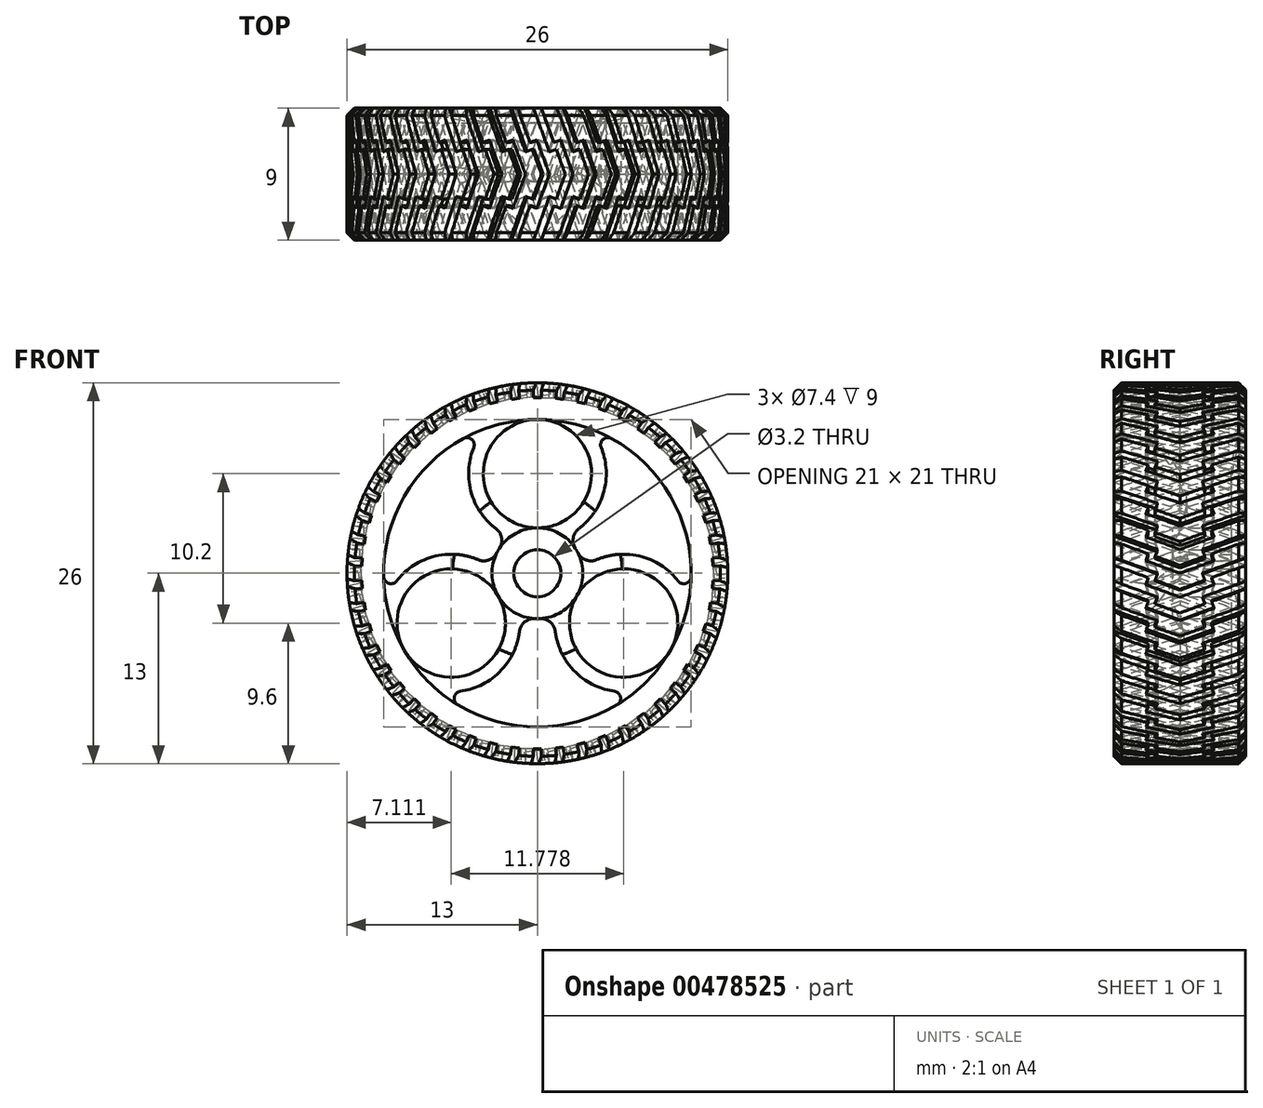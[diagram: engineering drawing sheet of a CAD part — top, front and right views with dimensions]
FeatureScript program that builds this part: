
annotation { "Feature Type Name" : "Feature", "Feature Type Description" : "" }
export const myFeature = defineFeature(function(context is Context, id is Id, definition is map)
    precondition{}
    {
        {
            var Q0;
            Q0=qCreatedBy(makeId("Right.planeOp"),FACE);
            var sketch = newSketch(context, id + "F0", { "sketchPlane" : qUnion([Q0])});
            skLineSegment(sketch, "E0", {"start": v(4.5, 13) * mm, "end": v(4.5, 10.5) * mm});
            skLineSegment(sketch, "E1", {"start": v(4.5, 10.5) * mm, "end": v(-4.5, 10.5) * mm});
            skLineSegment(sketch, "E2", {"start": v(-4.5, 10.5) * mm, "end": v(-4.5, 13) * mm});
            skLineSegment(sketch, "E3", {"start": v(-4.5, 13) * mm, "end": v(4.5, 13) * mm});
            skLineSegment(sketch, "E4", {"start": v(0, 4.58) * mm, "end": v(0, -2.9) * mm, "construction": true});
            skLineSegment(sketch, "E5", {"start": v(3.7, 0) * mm, "end": v(-3.86, 0) * mm, "construction": true});
            skLineSegment(sketch, "E6", {"start": v(3.5, 3.1) * mm, "end": v(3.5, 1.6) * mm});
            skLineSegment(sketch, "E7", {"start": v(3.5, 1.6) * mm, "end": v(0.5, 1.6) * mm});
            skLineSegment(sketch, "E8", {"start": v(0.5, 1.6) * mm, "end": v(0.5, 3.1) * mm});
            skLineSegment(sketch, "E9", {"start": v(0.5, 3.1) * mm, "end": v(3.5, 3.1) * mm});
            skSolve(sketch);
        }
        {
            var Q0;
            Q0=makeQuery(id+"F0.imprint","IMPRINT",FACE,{"disambiguationData":[TD([[makeQuery(id+"F0.imprint","IMPRINT",EDGE,{"derivedFrom":sQuery(id+"F0.wireOp",EDGE,"E0")}),-1.0]])]});
            var Q1;
            Q1=makeQuery(id+"F0.imprint","IMPRINT",FACE,{"disambiguationData":[TD([[makeQuery(id+"F0.imprint","IMPRINT",EDGE,{"derivedFrom":sQuery(id+"F0.wireOp",EDGE,"E6")}),-1.0]])]});
            var Q2;
            Q2=sQuery(id+"F0.wireOp",EDGE,"E5");
            revolve(context, id + "F1", {"entities" : qUnion([Q0, Q1]), "axis" : qUnion([Q2]), "revolveType" : RevolveType.FULL});
        }
        {
            var Q0;
            Q0=makeQuery(id+"F1.opRevolve","SWEPT_FACE",FACE,{"disambiguationData":[OSD([sQuery(id+"F0.wireOp",EDGE,"E6")])]});
            var sketch = newSketch(context, id + "F2", { "sketchPlane" : qUnion([Q0])});
            skCircle(sketch, "E10", {"center": v(0, 6.8) * mm, "radius": 4.7 * mm});
            skCircle(sketch, "E11", {"center": v(0, 6.8) * mm, "radius": 3.7 * mm});
            skLineSegment(sketch, "E12", {"start": v(5.5, 10.5) * mm, "end": v(-6.08, 10.5) * mm, "construction": true});
            skLineSegment(sketch, "E13", {"start": v(-5.55, 11.5) * mm, "end": v(4.86, 11.5) * mm, "construction": true});
            skSolve(sketch);
        }
        {
            var Q0;
            {var subQ4=sQuery(id+"F2.wireOp",EDGE,"E11");Q0=makeQuery(id+"F2.imprint","IMPRINT",FACE,{"disambiguationData":[TD([[makeQuery(id+"F2.imprint","IMPRINT",EDGE,{"derivedFrom":subQ4}),-1.0]])]});}
            var Q1;
            {var subQ0=sQuery(id+"F2.wireOp",EDGE,"E10");var subQ1=makeQuery(id+"F1.opRevolve","SWEPT_EDGE",EDGE,{"disambiguationData":[OSD([sQuery(id+"F0.wireOp",EDGE,"E6"),sQuery(id+"F0.wireOp",EDGE,"E9")])]});var subQ2=makeQuery(id+"F2.imprint","INTERSECT",VERTEX,{"disambiguationData":[OD(0.0)],"derivedFrom":[subQ1,subQ0]});Q1=makeQuery(id+"F2.imprint","IMPRINT",FACE,{"disambiguationData":[TD([[makeQuery(id+"F2.imprint","IMPRINT",EDGE,{"disambiguationData":[TD([[subQ2,1.0]])],"derivedFrom":subQ0}),1.0]])]});}
            var Q2;
            Q2=makeQuery(id+"F1.opRevolve","SWEPT_FACE",FACE,{"disambiguationData":[OSD([sQuery(id+"F0.wireOp",EDGE,"E8")])]});
            extrude(context, id + "F3", {"entities" : qUnion([Q0, Q1]), "endBound" : BoundingType.UP_TO_SURFACE, "oppositeDirection" : true, "endBoundEntityFace" : qUnion([Q2]), "depth" : 5 * mm});
        }
        {
            var Q0;
            Q0=makeQuery(id+"F3.opExtrude","SWEPT_BODY",BODY,{"disambiguationData":[OSD([sQuery(id+"F2.wireOp",EDGE,"E10"),sQuery(id+"F2.wireOp",EDGE,"E11")])]});
            var Q1;
            Q1=makeQuery(id+"F1.opRevolve","SWEPT_FACE",FACE,{"disambiguationData":[OSD([sQuery(id+"F0.wireOp",EDGE,"E9")])]});
            circularPattern(context, id + "F4", {"entities" : qUnion([Q0]), "axis" : qUnion([Q1]), "angle" : 360 * degree, "instanceCount" : 3, "equalSpace" : true});
        }
        {
            var Q0;
            Q0=makeQuery(id+"F3.opExtrude","SWEPT_BODY",BODY,{"disambiguationData":[OSD([sQuery(id+"F2.wireOp",EDGE,"E10"),sQuery(id+"F2.wireOp",EDGE,"E11")])]});
            var Q1;
            Q1=makeQuery(id+"F4.opPattern","COPY",BODY,{"derivedFrom":makeQuery(id+"F3.opExtrude","SWEPT_BODY",BODY,{"disambiguationData":[OSD([sQuery(id+"F2.wireOp",EDGE,"E10"),sQuery(id+"F2.wireOp",EDGE,"E11")])]}),"instanceName":"4"});
            var Q2;
            Q2=makeQuery(id+"F4.opPattern","COPY",BODY,{"derivedFrom":makeQuery(id+"F3.opExtrude","SWEPT_BODY",BODY,{"disambiguationData":[OSD([sQuery(id+"F2.wireOp",EDGE,"E10"),sQuery(id+"F2.wireOp",EDGE,"E11")])]}),"instanceName":"3"});
            var Q3;
            Q3=makeQuery(id+"F4.opPattern","COPY",BODY,{"derivedFrom":makeQuery(id+"F3.opExtrude","SWEPT_BODY",BODY,{"disambiguationData":[OSD([sQuery(id+"F2.wireOp",EDGE,"E10"),sQuery(id+"F2.wireOp",EDGE,"E11")])]}),"instanceName":"2"});
            var Q4;
            Q4=makeQuery(id+"F4.opPattern","COPY",BODY,{"derivedFrom":makeQuery(id+"F3.opExtrude","SWEPT_BODY",BODY,{"disambiguationData":[OSD([sQuery(id+"F2.wireOp",EDGE,"E10"),sQuery(id+"F2.wireOp",EDGE,"E11")])]}),"instanceName":"1"});
            var Q5;
            Q5=makeQuery(id+"F1.opRevolve","SWEPT_BODY",BODY,{"disambiguationData":[OSD([sQuery(id+"F0.wireOp",EDGE,"E6"),sQuery(id+"F0.wireOp",EDGE,"E7"),sQuery(id+"F0.wireOp",EDGE,"E8"),sQuery(id+"F0.wireOp",EDGE,"E9")])]});
            booleanBodies(context, id + "F5", {"operationType" : BooleanOperationType.UNION, "tools" : qUnion([Q0, Q1, Q2, Q3, Q4, Q5])});
        }
        {
            var Q0;
            Q0=makeQuery(id+"F3.opExtrude","SWEPT_BODY",BODY,{"disambiguationData":[OSD([sQuery(id+"F2.wireOp",EDGE,"E10"),sQuery(id+"F2.wireOp",EDGE,"E11")])]});
            var Q1;
            Q1=makeQuery(id+"F1.opRevolve","SWEPT_BODY",BODY,{"disambiguationData":[OSD([sQuery(id+"F0.wireOp",EDGE,"E0"),sQuery(id+"F0.wireOp",EDGE,"E1"),sQuery(id+"F0.wireOp",EDGE,"E2"),sQuery(id+"F0.wireOp",EDGE,"E3")])]});
            booleanBodies(context, id + "F6", {"operationType" : BooleanOperationType.UNION, "tools" : qUnion([Q0, Q1])});
        }
        {
            var Q0;
            {var subQ0=sQuery(id+"F0.wireOp",EDGE,"E0");var subQ1=sQuery(id+"F0.wireOp",EDGE,"E3");Q0=makeQuery(id+"F11.boolean.opBoolean","SPLIT",EDGE,{"disambiguationData":[TD([makeQuery(id+"F11.opPattern","COPY",FACE,{"derivedFrom":makeQuery(id+"F10.opExtrude","SWEPT_FACE",FACE,{"disambiguationData":[OSD([sQuery(id+"F9.wireOp",EDGE,"E14")])]}),"instanceName":"47"})])],"derivedFrom":makeQuery(id+"F1.opRevolve","SWEPT_EDGE",EDGE,{"disambiguationData":[OSD([subQ0,subQ1])]})});}
            var Q1;
            Q1=makeQuery(id+"F1.opRevolve","SWEPT_EDGE",EDGE,{"disambiguationData":[OSD([sQuery(id+"F0.wireOp",EDGE,"E2"),sQuery(id+"F0.wireOp",EDGE,"E3")])]});
            chamfer(context, id + "F7", {"entities" : qUnion([Q0, Q1]), "width" : .5 * mm, "tangentPropagation" : true});
        }
        {
            var Q0;
            Q0=qCreatedBy(makeId("Top.planeOp"),FACE);
            cPlane(context, id + "F8", {"entities" : qUnion([Q0]), "cplaneType" : CPlaneType.OFFSET, "offset" : 26 / 2 * mm, "width" : 150 * mm, "height" : 150 * mm});
        }
        {
            var Q0;
            Q0=qCreatedBy(id+"F8.planeOp",FACE);
            var sketch = newSketch(context, id + "F9", { "sketchPlane" : qUnion([Q0])});
            skLineSegment(sketch, "E14", {"start": v(0.27, 4.5) * mm, "end": v(1.12, 2.16) * mm});
            skLineSegment(sketch, "E15", {"start": v(1.59, 2.34) * mm, "end": v(1.12, 2.16) * mm});
            skLineSegment(sketch, "E16", {"start": v(1.59, 2.34) * mm, "end": v(2.44, 0) * mm});
            skLineSegment(sketch, "E17", {"start": v(-13.36, 0) * mm, "end": v(12.93, 0) * mm, "construction": true});
            skLineSegment(sketch, "E18", {"start": v(-0.27, 4.5) * mm, "end": v(0.82, 1.52) * mm});
            skLineSegment(sketch, "E19", {"start": v(0.82, 1.52) * mm, "end": v(1.29, 1.7) * mm});
            skLineSegment(sketch, "E20", {"start": v(1.29, 1.7) * mm, "end": v(1.9, 0) * mm});
            skLineSegment(sketch, "E21", {"start": v(-0.27, 4.5) * mm, "end": v(0.27, 4.5) * mm});
            skPoint(sketch, "E22", {"position": v(0, 4.5) * mm});
            skLineSegment(sketch, "E23.MirrorCS", {"start": v(1.59, -2.34) * mm, "end": v(2.44, 0) * mm});
            skLineSegment(sketch, "E24.MirrorCS", {"start": v(1.29, -1.7) * mm, "end": v(1.9, 0) * mm});
            skLineSegment(sketch, "E25.MirrorCS", {"start": v(0.82, -1.52) * mm, "end": v(1.29, -1.7) * mm});
            skLineSegment(sketch, "E26.MirrorCS", {"start": v(1.59, -2.34) * mm, "end": v(1.12, -2.16) * mm});
            skLineSegment(sketch, "E27.MirrorCS", {"start": v(0.27, -4.5) * mm, "end": v(1.12, -2.16) * mm});
            skLineSegment(sketch, "E28.MirrorCS", {"start": v(-0.27, -4.5) * mm, "end": v(0.82, -1.52) * mm});
            skLineSegment(sketch, "E29.MirrorCS", {"start": v(-0.27, -4.5) * mm, "end": v(0.27, -4.5) * mm});
            skLineSegment(sketch, "E30.0", {"start": v(-12.5, 4.5) * mm, "end": v(12.5, 4.5) * mm});
            skLineSegment(sketch, "E31.0", {"start": v(12.5, -4.5) * mm, "end": v(-12.5, -4.5) * mm});
            skSolve(sketch);
        }
        {
            var Q0;
            Q0=makeQuery(id+"F9.imprint","IMPRINT",FACE,{"disambiguationData":[TD([[makeQuery(id+"F9.imprint","IMPRINT",EDGE,{"derivedFrom":sQuery(id+"F9.wireOp",EDGE,"E14")}),-1.0]])]});
            extrude(context, id + "F10", {"entities" : qUnion([Q0]), "oppositeDirection" : true, "depth" : 1 * mm});
        }
        {
            var Q0;
            Q0=makeQuery(id+"F10.opExtrude","SWEPT_BODY",BODY,{"disambiguationData":[OSD([sQuery(id+"F9.wireOp",EDGE,"E14"),sQuery(id+"F9.wireOp",EDGE,"E15"),sQuery(id+"F9.wireOp",EDGE,"E16"),sQuery(id+"F9.wireOp",EDGE,"E18"),sQuery(id+"F9.wireOp",EDGE,"E19"),sQuery(id+"F9.wireOp",EDGE,"E20"),sQuery(id+"F9.wireOp",EDGE,"E21"),sQuery(id+"F9.wireOp",EDGE,"E23.MirrorCS"),sQuery(id+"F9.wireOp",EDGE,"E24.MirrorCS"),sQuery(id+"F9.wireOp",EDGE,"E25.MirrorCS"),sQuery(id+"F9.wireOp",EDGE,"E26.MirrorCS"),sQuery(id+"F9.wireOp",EDGE,"E27.MirrorCS"),sQuery(id+"F9.wireOp",EDGE,"E28.MirrorCS"),sQuery(id+"F9.wireOp",EDGE,"E29.MirrorCS")])]});
            var Q1;
            Q1=makeQuery(id+"F1.opRevolve","SWEPT_FACE",FACE,{"disambiguationData":[OSD([sQuery(id+"F0.wireOp",EDGE,"E3")])]});
            var Q2;
            Q2=makeQuery(id+"F3.opExtrude","SWEPT_BODY",BODY,{"disambiguationData":[OSD([sQuery(id+"F2.wireOp",EDGE,"E10"),sQuery(id+"F2.wireOp",EDGE,"E11")])]});
            circularPattern(context, id + "F11", {"operationType" : NewBodyOperationType.REMOVE, "entities" : qUnion([Q0]), "axis" : qUnion([Q1]), "angle" : 360 * degree, "instanceCount" : 50, "equalSpace" : true});
        }
        {
            var Q0;
            {var subQ0=sQuery(id+"F0.wireOp",EDGE,"E8");var subQ1=makeQuery(id+"F3.opExtrude","CAP_FACE",FACE,{"disambiguationData":[OSD([subQ0])],"isStart":false});Q0=makeQuery(id+"F5.opBoolean","MERGE",FACE,{"derivedFrom":[makeQuery(id+"F1.opRevolve","SWEPT_FACE",FACE,{"disambiguationData":[OSD([subQ0])]}),subQ1,makeQuery(id+"F4.opPattern","COPY",FACE,{"derivedFrom":subQ1,"instanceName":"1"}),makeQuery(id+"F4.opPattern","COPY",FACE,{"derivedFrom":subQ1,"instanceName":"2"}),makeQuery(id+"F4.opPattern","COPY",FACE,{"derivedFrom":subQ1,"instanceName":"3"}),makeQuery(id+"F4.opPattern","COPY",FACE,{"derivedFrom":subQ1,"instanceName":"4"})]});}
            var sketch = newSketch(context, id + "F12", { "sketchPlane" : qUnion([Q0])});
            skCircle(sketch, "E32", {"center": v(0, 0) * mm, "radius": 1.6 * mm});
            skCircle(sketch, "E33", {"center": v(0, 0) * mm, "radius": 3.1 * mm});
            skSolve(sketch);
        }
        {
            var Q0;
            Q0=makeQuery(id+"F12.imprint","IMPRINT",FACE,{"disambiguationData":[TD([[makeQuery(id+"F12.imprint","IMPRINT",EDGE,{"derivedFrom":sQuery(id+"F12.wireOp",EDGE,"E32")}),1.0]])]});
            extrude(context, id + "F13", {"entities" : qUnion([Q0]), "operationType" : NewBodyOperationType.ADD, "depth" : 1 * mm});
        }
        {
            var Q0;
            Q0=makeQuery(id+"F6.opBoolean","INTERSECT",EDGE,{"disambiguationData":[OD(0.0)],"derivedFrom":[makeQuery(id+"F1.opRevolve","SWEPT_FACE",FACE,{"disambiguationData":[OSD([sQuery(id+"F0.wireOp",EDGE,"E1")])]}),makeQuery(id+"F4.opPattern","COPY",FACE,{"derivedFrom":makeQuery(id+"F3.opExtrude","SWEPT_FACE",FACE,{"disambiguationData":[OSD([sQuery(id+"F2.wireOp",EDGE,"E10")])]}),"instanceName":"2"})]});
            var Q1;
            Q1=makeQuery(id+"F6.opBoolean","INTERSECT",EDGE,{"disambiguationData":[OD(1.0)],"derivedFrom":[makeQuery(id+"F1.opRevolve","SWEPT_FACE",FACE,{"disambiguationData":[OSD([sQuery(id+"F0.wireOp",EDGE,"E1")])]}),makeQuery(id+"F4.opPattern","COPY",FACE,{"derivedFrom":makeQuery(id+"F3.opExtrude","SWEPT_FACE",FACE,{"disambiguationData":[OSD([sQuery(id+"F2.wireOp",EDGE,"E10")])]}),"instanceName":"2"})]});
            var Q2;
            Q2=makeQuery(id+"F6.opBoolean","INTERSECT",EDGE,{"disambiguationData":[OD(1.0)],"derivedFrom":[makeQuery(id+"F1.opRevolve","SWEPT_FACE",FACE,{"disambiguationData":[OSD([sQuery(id+"F0.wireOp",EDGE,"E1")])]}),makeQuery(id+"F4.opPattern","COPY",FACE,{"derivedFrom":makeQuery(id+"F3.opExtrude","SWEPT_FACE",FACE,{"disambiguationData":[OSD([sQuery(id+"F2.wireOp",EDGE,"E10")])]}),"instanceName":"1"})]});
            var Q3;
            Q3=makeQuery(id+"F6.opBoolean","INTERSECT",EDGE,{"disambiguationData":[OD(0.0)],"derivedFrom":[makeQuery(id+"F1.opRevolve","SWEPT_FACE",FACE,{"disambiguationData":[OSD([sQuery(id+"F0.wireOp",EDGE,"E1")])]}),makeQuery(id+"F3.opExtrude","SWEPT_FACE",FACE,{"disambiguationData":[OSD([sQuery(id+"F2.wireOp",EDGE,"E10")])]})]});
            var Q4;
            Q4=makeQuery(id+"F6.opBoolean","INTERSECT",EDGE,{"disambiguationData":[OD(1.0)],"derivedFrom":[makeQuery(id+"F1.opRevolve","SWEPT_FACE",FACE,{"disambiguationData":[OSD([sQuery(id+"F0.wireOp",EDGE,"E1")])]}),makeQuery(id+"F3.opExtrude","SWEPT_FACE",FACE,{"disambiguationData":[OSD([sQuery(id+"F2.wireOp",EDGE,"E10")])]})]});
            var Q5;
            Q5=makeQuery(id+"F6.opBoolean","INTERSECT",EDGE,{"disambiguationData":[OD(0.0)],"derivedFrom":[makeQuery(id+"F1.opRevolve","SWEPT_FACE",FACE,{"disambiguationData":[OSD([sQuery(id+"F0.wireOp",EDGE,"E1")])]}),makeQuery(id+"F4.opPattern","COPY",FACE,{"derivedFrom":makeQuery(id+"F3.opExtrude","SWEPT_FACE",FACE,{"disambiguationData":[OSD([sQuery(id+"F2.wireOp",EDGE,"E10")])]}),"instanceName":"1"})]});
            fillet(context, id + "F14", {"entities" : qUnion([Q0, Q1, Q2, Q3, Q4, Q5]), "radius" : .5 * mm, "tangentPropagation" : true, "allowEdgeOverflow" : false});
        }
        {
            var Q0;
            Q0=makeQuery(id+"F5.opBoolean","INTERSECT",EDGE,{"disambiguationData":[OD(0.0)],"derivedFrom":[makeQuery(id+"F1.opRevolve","SWEPT_FACE",FACE,{"disambiguationData":[OSD([sQuery(id+"F0.wireOp",EDGE,"E9")])]}),makeQuery(id+"F4.opPattern","COPY",FACE,{"derivedFrom":makeQuery(id+"F3.opExtrude","SWEPT_FACE",FACE,{"disambiguationData":[OSD([sQuery(id+"F2.wireOp",EDGE,"E10")])]}),"instanceName":"1"})]});
            var Q1;
            Q1=makeQuery(id+"F5.opBoolean","INTERSECT",EDGE,{"disambiguationData":[OD(1.0)],"derivedFrom":[makeQuery(id+"F1.opRevolve","SWEPT_FACE",FACE,{"disambiguationData":[OSD([sQuery(id+"F0.wireOp",EDGE,"E9")])]}),makeQuery(id+"F4.opPattern","COPY",FACE,{"derivedFrom":makeQuery(id+"F3.opExtrude","SWEPT_FACE",FACE,{"disambiguationData":[OSD([sQuery(id+"F2.wireOp",EDGE,"E10")])]}),"instanceName":"1"})]});
            var Q2;
            Q2=makeQuery(id+"F5.opBoolean","INTERSECT",EDGE,{"disambiguationData":[OD(1.0)],"derivedFrom":[makeQuery(id+"F1.opRevolve","SWEPT_FACE",FACE,{"disambiguationData":[OSD([sQuery(id+"F0.wireOp",EDGE,"E9")])]}),makeQuery(id+"F3.opExtrude","SWEPT_FACE",FACE,{"disambiguationData":[OSD([sQuery(id+"F2.wireOp",EDGE,"E10")])]})]});
            var Q3;
            Q3=makeQuery(id+"F5.opBoolean","INTERSECT",EDGE,{"disambiguationData":[OD(0.0)],"derivedFrom":[makeQuery(id+"F1.opRevolve","SWEPT_FACE",FACE,{"disambiguationData":[OSD([sQuery(id+"F0.wireOp",EDGE,"E9")])]}),makeQuery(id+"F4.opPattern","COPY",FACE,{"derivedFrom":makeQuery(id+"F3.opExtrude","SWEPT_FACE",FACE,{"disambiguationData":[OSD([sQuery(id+"F2.wireOp",EDGE,"E10")])]}),"instanceName":"2"})]});
            var Q4;
            Q4=makeQuery(id+"F5.opBoolean","INTERSECT",EDGE,{"disambiguationData":[OD(1.0)],"derivedFrom":[makeQuery(id+"F1.opRevolve","SWEPT_FACE",FACE,{"disambiguationData":[OSD([sQuery(id+"F0.wireOp",EDGE,"E9")])]}),makeQuery(id+"F4.opPattern","COPY",FACE,{"derivedFrom":makeQuery(id+"F3.opExtrude","SWEPT_FACE",FACE,{"disambiguationData":[OSD([sQuery(id+"F2.wireOp",EDGE,"E10")])]}),"instanceName":"2"})]});
            var Q5;
            Q5=makeQuery(id+"F5.opBoolean","INTERSECT",EDGE,{"disambiguationData":[OD(0.0)],"derivedFrom":[makeQuery(id+"F1.opRevolve","SWEPT_FACE",FACE,{"disambiguationData":[OSD([sQuery(id+"F0.wireOp",EDGE,"E9")])]}),makeQuery(id+"F3.opExtrude","SWEPT_FACE",FACE,{"disambiguationData":[OSD([sQuery(id+"F2.wireOp",EDGE,"E10")])]})]});
            fillet(context, id + "F15", {"entities" : qUnion([Q0, Q1, Q2, Q3, Q4, Q5]), "radius" : 1 * mm, "tangentPropagation" : true, "allowEdgeOverflow" : false});
        }
        {
            var Q0;
            {var subQ0=sQuery(id+"F0.wireOp",EDGE,"E8");var subQ1=makeQuery(id+"F3.opExtrude","CAP_FACE",FACE,{"disambiguationData":[OSD([subQ0])],"isStart":false});var subQ2=sQuery(id+"F12.wireOp",EDGE,"E33");Q0=makeQuery(id+"F13.boolean.opBoolean","SPLIT",EDGE,{"disambiguationData":[TD([makeQuery(id+"F1.opRevolve","SWEPT_FACE",FACE,{"disambiguationData":[OSD([subQ0])]}),makeQuery(id+"F1.opRevolve","SWEPT_FACE",FACE,{"disambiguationData":[OSD([sQuery(id+"F0.wireOp",EDGE,"E9")])]}),subQ1,makeQuery(id+"F4.opPattern","COPY",FACE,{"derivedFrom":subQ1,"instanceName":"1"}),makeQuery(id+"F4.opPattern","COPY",FACE,{"derivedFrom":subQ1,"instanceName":"2"}),makeQuery(id+"F4.opPattern","COPY",FACE,{"derivedFrom":makeQuery(id+"F3.opExtrude","SWEPT_FACE",FACE,{"disambiguationData":[OSD([sQuery(id+"F2.wireOp",EDGE,"E10")])]}),"instanceName":"2"}),makeQuery(id+"F4.opPattern","COPY",FACE,{"derivedFrom":makeQuery(id+"F3.opExtrude","SWEPT_FACE",FACE,{"disambiguationData":[OSD([sQuery(id+"F2.wireOp",EDGE,"E11")])]}),"instanceName":"2"}),makeQuery(id+"F13.opExtrude","SWEPT_FACE",FACE,{"disambiguationData":[OSD([subQ2])]})]),OD(1.0)],"derivedFrom":makeQuery(id+"F13.opExtrude","CAP_EDGE",EDGE,{"disambiguationData":[OSD([subQ2])],"isStart":true})});}
            var Q1;
            {var subQ0=sQuery(id+"F0.wireOp",EDGE,"E8");var subQ1=makeQuery(id+"F3.opExtrude","CAP_FACE",FACE,{"disambiguationData":[OSD([subQ0])],"isStart":false});var subQ2=sQuery(id+"F12.wireOp",EDGE,"E33");Q1=makeQuery(id+"F13.boolean.opBoolean","SPLIT",EDGE,{"disambiguationData":[TD([makeQuery(id+"F1.opRevolve","SWEPT_FACE",FACE,{"disambiguationData":[OSD([subQ0])]}),makeQuery(id+"F1.opRevolve","SWEPT_FACE",FACE,{"disambiguationData":[OSD([sQuery(id+"F0.wireOp",EDGE,"E9")])]}),subQ1,makeQuery(id+"F4.opPattern","COPY",FACE,{"derivedFrom":subQ1,"instanceName":"1"}),makeQuery(id+"F4.opPattern","COPY",FACE,{"derivedFrom":subQ1,"instanceName":"2"}),makeQuery(id+"F4.opPattern","COPY",FACE,{"derivedFrom":makeQuery(id+"F3.opExtrude","SWEPT_FACE",FACE,{"disambiguationData":[OSD([sQuery(id+"F2.wireOp",EDGE,"E10")])]}),"instanceName":"2"}),makeQuery(id+"F4.opPattern","COPY",FACE,{"derivedFrom":makeQuery(id+"F3.opExtrude","SWEPT_FACE",FACE,{"disambiguationData":[OSD([sQuery(id+"F2.wireOp",EDGE,"E11")])]}),"instanceName":"2"}),makeQuery(id+"F13.opExtrude","SWEPT_FACE",FACE,{"disambiguationData":[OSD([subQ2])]})]),OD(0.0)],"derivedFrom":makeQuery(id+"F13.opExtrude","CAP_EDGE",EDGE,{"disambiguationData":[OSD([subQ2])],"isStart":true})});}
            var Q2;
            {var subQ0=sQuery(id+"F0.wireOp",EDGE,"E8");var subQ1=makeQuery(id+"F3.opExtrude","CAP_FACE",FACE,{"disambiguationData":[OSD([subQ0])],"isStart":false});var subQ2=sQuery(id+"F12.wireOp",EDGE,"E33");Q2=makeQuery(id+"F13.boolean.opBoolean","SPLIT",EDGE,{"disambiguationData":[TD([makeQuery(id+"F1.opRevolve","SWEPT_FACE",FACE,{"disambiguationData":[OSD([subQ0])]}),makeQuery(id+"F1.opRevolve","SWEPT_FACE",FACE,{"disambiguationData":[OSD([sQuery(id+"F0.wireOp",EDGE,"E9")])]}),subQ1,makeQuery(id+"F3.opExtrude","SWEPT_FACE",FACE,{"disambiguationData":[OSD([sQuery(id+"F2.wireOp",EDGE,"E10")])]}),makeQuery(id+"F3.opExtrude","SWEPT_FACE",FACE,{"disambiguationData":[OSD([sQuery(id+"F2.wireOp",EDGE,"E11")])]}),makeQuery(id+"F4.opPattern","COPY",FACE,{"derivedFrom":subQ1,"instanceName":"1"}),makeQuery(id+"F4.opPattern","COPY",FACE,{"derivedFrom":subQ1,"instanceName":"2"}),makeQuery(id+"F13.opExtrude","SWEPT_FACE",FACE,{"disambiguationData":[OSD([subQ2])]})]),OD(1.0)],"derivedFrom":makeQuery(id+"F13.opExtrude","CAP_EDGE",EDGE,{"disambiguationData":[OSD([subQ2])],"isStart":true})});}
            var Q3;
            {var subQ0=sQuery(id+"F0.wireOp",EDGE,"E8");var subQ1=makeQuery(id+"F3.opExtrude","CAP_FACE",FACE,{"disambiguationData":[OSD([subQ0])],"isStart":false});var subQ2=sQuery(id+"F12.wireOp",EDGE,"E33");Q3=makeQuery(id+"F13.boolean.opBoolean","SPLIT",EDGE,{"disambiguationData":[TD([makeQuery(id+"F1.opRevolve","SWEPT_FACE",FACE,{"disambiguationData":[OSD([subQ0])]}),makeQuery(id+"F1.opRevolve","SWEPT_FACE",FACE,{"disambiguationData":[OSD([sQuery(id+"F0.wireOp",EDGE,"E9")])]}),subQ1,makeQuery(id+"F3.opExtrude","SWEPT_FACE",FACE,{"disambiguationData":[OSD([sQuery(id+"F2.wireOp",EDGE,"E10")])]}),makeQuery(id+"F3.opExtrude","SWEPT_FACE",FACE,{"disambiguationData":[OSD([sQuery(id+"F2.wireOp",EDGE,"E11")])]}),makeQuery(id+"F4.opPattern","COPY",FACE,{"derivedFrom":subQ1,"instanceName":"1"}),makeQuery(id+"F4.opPattern","COPY",FACE,{"derivedFrom":subQ1,"instanceName":"2"}),makeQuery(id+"F13.opExtrude","SWEPT_FACE",FACE,{"disambiguationData":[OSD([subQ2])]})]),OD(0.0)],"derivedFrom":makeQuery(id+"F13.opExtrude","CAP_EDGE",EDGE,{"disambiguationData":[OSD([subQ2])],"isStart":true})});}
            var Q4;
            {var subQ0=sQuery(id+"F0.wireOp",EDGE,"E8");var subQ1=makeQuery(id+"F3.opExtrude","CAP_FACE",FACE,{"disambiguationData":[OSD([subQ0])],"isStart":false});var subQ2=sQuery(id+"F12.wireOp",EDGE,"E33");Q4=makeQuery(id+"F13.boolean.opBoolean","SPLIT",EDGE,{"disambiguationData":[TD([makeQuery(id+"F1.opRevolve","SWEPT_FACE",FACE,{"disambiguationData":[OSD([subQ0])]}),makeQuery(id+"F1.opRevolve","SWEPT_FACE",FACE,{"disambiguationData":[OSD([sQuery(id+"F0.wireOp",EDGE,"E9")])]}),subQ1,makeQuery(id+"F4.opPattern","COPY",FACE,{"derivedFrom":subQ1,"instanceName":"1"}),makeQuery(id+"F4.opPattern","COPY",FACE,{"derivedFrom":makeQuery(id+"F3.opExtrude","SWEPT_FACE",FACE,{"disambiguationData":[OSD([sQuery(id+"F2.wireOp",EDGE,"E10")])]}),"instanceName":"1"}),makeQuery(id+"F4.opPattern","COPY",FACE,{"derivedFrom":makeQuery(id+"F3.opExtrude","SWEPT_FACE",FACE,{"disambiguationData":[OSD([sQuery(id+"F2.wireOp",EDGE,"E11")])]}),"instanceName":"1"}),makeQuery(id+"F4.opPattern","COPY",FACE,{"derivedFrom":subQ1,"instanceName":"2"}),makeQuery(id+"F13.opExtrude","SWEPT_FACE",FACE,{"disambiguationData":[OSD([subQ2])]})]),OD(0.0)],"derivedFrom":makeQuery(id+"F13.opExtrude","CAP_EDGE",EDGE,{"disambiguationData":[OSD([subQ2])],"isStart":true})});}
            var Q5;
            {var subQ0=sQuery(id+"F0.wireOp",EDGE,"E8");var subQ1=makeQuery(id+"F3.opExtrude","CAP_FACE",FACE,{"disambiguationData":[OSD([subQ0])],"isStart":false});var subQ2=sQuery(id+"F12.wireOp",EDGE,"E33");Q5=makeQuery(id+"F13.boolean.opBoolean","SPLIT",EDGE,{"disambiguationData":[TD([makeQuery(id+"F1.opRevolve","SWEPT_FACE",FACE,{"disambiguationData":[OSD([subQ0])]}),makeQuery(id+"F1.opRevolve","SWEPT_FACE",FACE,{"disambiguationData":[OSD([sQuery(id+"F0.wireOp",EDGE,"E9")])]}),subQ1,makeQuery(id+"F4.opPattern","COPY",FACE,{"derivedFrom":subQ1,"instanceName":"1"}),makeQuery(id+"F4.opPattern","COPY",FACE,{"derivedFrom":makeQuery(id+"F3.opExtrude","SWEPT_FACE",FACE,{"disambiguationData":[OSD([sQuery(id+"F2.wireOp",EDGE,"E10")])]}),"instanceName":"1"}),makeQuery(id+"F4.opPattern","COPY",FACE,{"derivedFrom":makeQuery(id+"F3.opExtrude","SWEPT_FACE",FACE,{"disambiguationData":[OSD([sQuery(id+"F2.wireOp",EDGE,"E11")])]}),"instanceName":"1"}),makeQuery(id+"F4.opPattern","COPY",FACE,{"derivedFrom":subQ1,"instanceName":"2"}),makeQuery(id+"F13.opExtrude","SWEPT_FACE",FACE,{"disambiguationData":[OSD([subQ2])]})]),OD(1.0)],"derivedFrom":makeQuery(id+"F13.opExtrude","CAP_EDGE",EDGE,{"disambiguationData":[OSD([subQ2])],"isStart":true})});}
            var Q6;
            {var subQ0=sQuery(id+"F0.wireOp",EDGE,"E8");var subQ1=makeQuery(id+"F3.opExtrude","CAP_FACE",FACE,{"disambiguationData":[OSD([subQ0])],"isStart":false});Q6=makeQuery(id+"F6.opBoolean","INTERSECT",EDGE,{"disambiguationData":[OD(3.0)],"derivedFrom":[makeQuery(id+"F1.opRevolve","SWEPT_FACE",FACE,{"disambiguationData":[OSD([sQuery(id+"F0.wireOp",EDGE,"E1")])]}),makeQuery(id+"F5.opBoolean","MERGE",FACE,{"derivedFrom":[makeQuery(id+"F1.opRevolve","SWEPT_FACE",FACE,{"disambiguationData":[OSD([subQ0])]}),subQ1,makeQuery(id+"F4.opPattern","COPY",FACE,{"derivedFrom":subQ1,"instanceName":"1"}),makeQuery(id+"F4.opPattern","COPY",FACE,{"derivedFrom":subQ1,"instanceName":"2"})]})]});}
            var Q7;
            {var subQ0=sQuery(id+"F0.wireOp",EDGE,"E8");var subQ1=makeQuery(id+"F3.opExtrude","CAP_FACE",FACE,{"disambiguationData":[OSD([subQ0])],"isStart":false});Q7=makeQuery(id+"F6.opBoolean","INTERSECT",EDGE,{"disambiguationData":[OD(2.0)],"derivedFrom":[makeQuery(id+"F1.opRevolve","SWEPT_FACE",FACE,{"disambiguationData":[OSD([sQuery(id+"F0.wireOp",EDGE,"E1")])]}),makeQuery(id+"F5.opBoolean","MERGE",FACE,{"derivedFrom":[makeQuery(id+"F1.opRevolve","SWEPT_FACE",FACE,{"disambiguationData":[OSD([subQ0])]}),subQ1,makeQuery(id+"F4.opPattern","COPY",FACE,{"derivedFrom":subQ1,"instanceName":"1"}),makeQuery(id+"F4.opPattern","COPY",FACE,{"derivedFrom":subQ1,"instanceName":"2"})]})]});}
            var Q8;
            {var subQ0=sQuery(id+"F0.wireOp",EDGE,"E8");var subQ1=makeQuery(id+"F3.opExtrude","CAP_FACE",FACE,{"disambiguationData":[OSD([subQ0])],"isStart":false});Q8=makeQuery(id+"F6.opBoolean","INTERSECT",EDGE,{"disambiguationData":[OD(4.0)],"derivedFrom":[makeQuery(id+"F1.opRevolve","SWEPT_FACE",FACE,{"disambiguationData":[OSD([sQuery(id+"F0.wireOp",EDGE,"E1")])]}),makeQuery(id+"F5.opBoolean","MERGE",FACE,{"derivedFrom":[makeQuery(id+"F1.opRevolve","SWEPT_FACE",FACE,{"disambiguationData":[OSD([subQ0])]}),subQ1,makeQuery(id+"F4.opPattern","COPY",FACE,{"derivedFrom":subQ1,"instanceName":"1"}),makeQuery(id+"F4.opPattern","COPY",FACE,{"derivedFrom":subQ1,"instanceName":"2"})]})]});}
            var Q9;
            {var subQ0=sQuery(id+"F0.wireOp",EDGE,"E8");var subQ1=makeQuery(id+"F3.opExtrude","CAP_FACE",FACE,{"disambiguationData":[OSD([subQ0])],"isStart":false});Q9=makeQuery(id+"F6.opBoolean","INTERSECT",EDGE,{"disambiguationData":[OD(5.0)],"derivedFrom":[makeQuery(id+"F1.opRevolve","SWEPT_FACE",FACE,{"disambiguationData":[OSD([sQuery(id+"F0.wireOp",EDGE,"E1")])]}),makeQuery(id+"F5.opBoolean","MERGE",FACE,{"derivedFrom":[makeQuery(id+"F1.opRevolve","SWEPT_FACE",FACE,{"disambiguationData":[OSD([subQ0])]}),subQ1,makeQuery(id+"F4.opPattern","COPY",FACE,{"derivedFrom":subQ1,"instanceName":"1"}),makeQuery(id+"F4.opPattern","COPY",FACE,{"derivedFrom":subQ1,"instanceName":"2"})]})]});}
            var Q10;
            {var subQ0=sQuery(id+"F0.wireOp",EDGE,"E8");var subQ1=makeQuery(id+"F3.opExtrude","CAP_FACE",FACE,{"disambiguationData":[OSD([subQ0])],"isStart":false});Q10=makeQuery(id+"F6.opBoolean","INTERSECT",EDGE,{"disambiguationData":[OD(1.0)],"derivedFrom":[makeQuery(id+"F1.opRevolve","SWEPT_FACE",FACE,{"disambiguationData":[OSD([sQuery(id+"F0.wireOp",EDGE,"E1")])]}),makeQuery(id+"F5.opBoolean","MERGE",FACE,{"derivedFrom":[makeQuery(id+"F1.opRevolve","SWEPT_FACE",FACE,{"disambiguationData":[OSD([subQ0])]}),subQ1,makeQuery(id+"F4.opPattern","COPY",FACE,{"derivedFrom":subQ1,"instanceName":"1"}),makeQuery(id+"F4.opPattern","COPY",FACE,{"derivedFrom":subQ1,"instanceName":"2"})]})]});}
            var Q11;
            {var subQ0=sQuery(id+"F0.wireOp",EDGE,"E8");var subQ1=makeQuery(id+"F3.opExtrude","CAP_FACE",FACE,{"disambiguationData":[OSD([subQ0])],"isStart":false});Q11=makeQuery(id+"F6.opBoolean","INTERSECT",EDGE,{"disambiguationData":[OD(0.0)],"derivedFrom":[makeQuery(id+"F1.opRevolve","SWEPT_FACE",FACE,{"disambiguationData":[OSD([sQuery(id+"F0.wireOp",EDGE,"E1")])]}),makeQuery(id+"F5.opBoolean","MERGE",FACE,{"derivedFrom":[makeQuery(id+"F1.opRevolve","SWEPT_FACE",FACE,{"disambiguationData":[OSD([subQ0])]}),subQ1,makeQuery(id+"F4.opPattern","COPY",FACE,{"derivedFrom":subQ1,"instanceName":"1"}),makeQuery(id+"F4.opPattern","COPY",FACE,{"derivedFrom":subQ1,"instanceName":"2"})]})]});}
            fillet(context, id + "F16", {"entities" : qUnion([Q0, Q1, Q2, Q3, Q4, Q5, Q6, Q7, Q8, Q9, Q10, Q11]), "radius" : 5 * mm, "tangentPropagation" : true, "allowEdgeOverflow" : false});
        }
        {
            var Q0;
            {var subQ0=makeQuery(id+"F3.opExtrude","CAP_FACE",FACE,{"disambiguationData":[OSD([sQuery(id+"F2.wireOp",EDGE,"E10"),sQuery(id+"F2.wireOp",EDGE,"E11")])],"isStart":true});Q0=makeQuery(id+"F6.opBoolean","INTERSECT",EDGE,{"disambiguationData":[OD(3.0)],"derivedFrom":[makeQuery(id+"F1.opRevolve","SWEPT_FACE",FACE,{"disambiguationData":[OSD([sQuery(id+"F0.wireOp",EDGE,"E1")])]}),makeQuery(id+"F5.opBoolean","MERGE",FACE,{"derivedFrom":[makeQuery(id+"F1.opRevolve","SWEPT_FACE",FACE,{"disambiguationData":[OSD([sQuery(id+"F0.wireOp",EDGE,"E6")])]}),subQ0,makeQuery(id+"F4.opPattern","COPY",FACE,{"derivedFrom":subQ0,"instanceName":"1"}),makeQuery(id+"F4.opPattern","COPY",FACE,{"derivedFrom":subQ0,"instanceName":"2"})]})]});}
            var Q1;
            {var subQ0=makeQuery(id+"F3.opExtrude","CAP_FACE",FACE,{"disambiguationData":[OSD([sQuery(id+"F2.wireOp",EDGE,"E10"),sQuery(id+"F2.wireOp",EDGE,"E11")])],"isStart":true});Q1=makeQuery(id+"F6.opBoolean","INTERSECT",EDGE,{"disambiguationData":[OD(2.0)],"derivedFrom":[makeQuery(id+"F1.opRevolve","SWEPT_FACE",FACE,{"disambiguationData":[OSD([sQuery(id+"F0.wireOp",EDGE,"E1")])]}),makeQuery(id+"F5.opBoolean","MERGE",FACE,{"derivedFrom":[makeQuery(id+"F1.opRevolve","SWEPT_FACE",FACE,{"disambiguationData":[OSD([sQuery(id+"F0.wireOp",EDGE,"E6")])]}),subQ0,makeQuery(id+"F4.opPattern","COPY",FACE,{"derivedFrom":subQ0,"instanceName":"1"}),makeQuery(id+"F4.opPattern","COPY",FACE,{"derivedFrom":subQ0,"instanceName":"2"})]})]});}
            var Q2;
            {var subQ0=makeQuery(id+"F3.opExtrude","CAP_FACE",FACE,{"disambiguationData":[OSD([sQuery(id+"F2.wireOp",EDGE,"E10"),sQuery(id+"F2.wireOp",EDGE,"E11")])],"isStart":true});Q2=makeQuery(id+"F6.opBoolean","INTERSECT",EDGE,{"disambiguationData":[OD(0.0)],"derivedFrom":[makeQuery(id+"F1.opRevolve","SWEPT_FACE",FACE,{"disambiguationData":[OSD([sQuery(id+"F0.wireOp",EDGE,"E1")])]}),makeQuery(id+"F5.opBoolean","MERGE",FACE,{"derivedFrom":[makeQuery(id+"F1.opRevolve","SWEPT_FACE",FACE,{"disambiguationData":[OSD([sQuery(id+"F0.wireOp",EDGE,"E6")])]}),subQ0,makeQuery(id+"F4.opPattern","COPY",FACE,{"derivedFrom":subQ0,"instanceName":"1"}),makeQuery(id+"F4.opPattern","COPY",FACE,{"derivedFrom":subQ0,"instanceName":"2"})]})]});}
            var Q3;
            {var subQ0=makeQuery(id+"F3.opExtrude","CAP_FACE",FACE,{"disambiguationData":[OSD([sQuery(id+"F2.wireOp",EDGE,"E10"),sQuery(id+"F2.wireOp",EDGE,"E11")])],"isStart":true});Q3=makeQuery(id+"F6.opBoolean","INTERSECT",EDGE,{"disambiguationData":[OD(1.0)],"derivedFrom":[makeQuery(id+"F1.opRevolve","SWEPT_FACE",FACE,{"disambiguationData":[OSD([sQuery(id+"F0.wireOp",EDGE,"E1")])]}),makeQuery(id+"F5.opBoolean","MERGE",FACE,{"derivedFrom":[makeQuery(id+"F1.opRevolve","SWEPT_FACE",FACE,{"disambiguationData":[OSD([sQuery(id+"F0.wireOp",EDGE,"E6")])]}),subQ0,makeQuery(id+"F4.opPattern","COPY",FACE,{"derivedFrom":subQ0,"instanceName":"1"}),makeQuery(id+"F4.opPattern","COPY",FACE,{"derivedFrom":subQ0,"instanceName":"2"})]})]});}
            var Q4;
            {var subQ0=makeQuery(id+"F3.opExtrude","CAP_FACE",FACE,{"disambiguationData":[OSD([sQuery(id+"F2.wireOp",EDGE,"E10"),sQuery(id+"F2.wireOp",EDGE,"E11")])],"isStart":true});Q4=makeQuery(id+"F6.opBoolean","INTERSECT",EDGE,{"disambiguationData":[OD(4.0)],"derivedFrom":[makeQuery(id+"F1.opRevolve","SWEPT_FACE",FACE,{"disambiguationData":[OSD([sQuery(id+"F0.wireOp",EDGE,"E1")])]}),makeQuery(id+"F5.opBoolean","MERGE",FACE,{"derivedFrom":[makeQuery(id+"F1.opRevolve","SWEPT_FACE",FACE,{"disambiguationData":[OSD([sQuery(id+"F0.wireOp",EDGE,"E6")])]}),subQ0,makeQuery(id+"F4.opPattern","COPY",FACE,{"derivedFrom":subQ0,"instanceName":"1"}),makeQuery(id+"F4.opPattern","COPY",FACE,{"derivedFrom":subQ0,"instanceName":"2"})]})]});}
            var Q5;
            {var subQ0=makeQuery(id+"F3.opExtrude","CAP_FACE",FACE,{"disambiguationData":[OSD([sQuery(id+"F2.wireOp",EDGE,"E10"),sQuery(id+"F2.wireOp",EDGE,"E11")])],"isStart":true});Q5=makeQuery(id+"F6.opBoolean","INTERSECT",EDGE,{"disambiguationData":[OD(5.0)],"derivedFrom":[makeQuery(id+"F1.opRevolve","SWEPT_FACE",FACE,{"disambiguationData":[OSD([sQuery(id+"F0.wireOp",EDGE,"E1")])]}),makeQuery(id+"F5.opBoolean","MERGE",FACE,{"derivedFrom":[makeQuery(id+"F1.opRevolve","SWEPT_FACE",FACE,{"disambiguationData":[OSD([sQuery(id+"F0.wireOp",EDGE,"E6")])]}),subQ0,makeQuery(id+"F4.opPattern","COPY",FACE,{"derivedFrom":subQ0,"instanceName":"1"}),makeQuery(id+"F4.opPattern","COPY",FACE,{"derivedFrom":subQ0,"instanceName":"2"})]})]});}
            fillet(context, id + "F17", {"entities" : qUnion([Q0, Q1, Q2, Q3, Q4, Q5]), "radius" : 5 * mm, "tangentPropagation" : true, "allowEdgeOverflow" : false});
        }
    });
